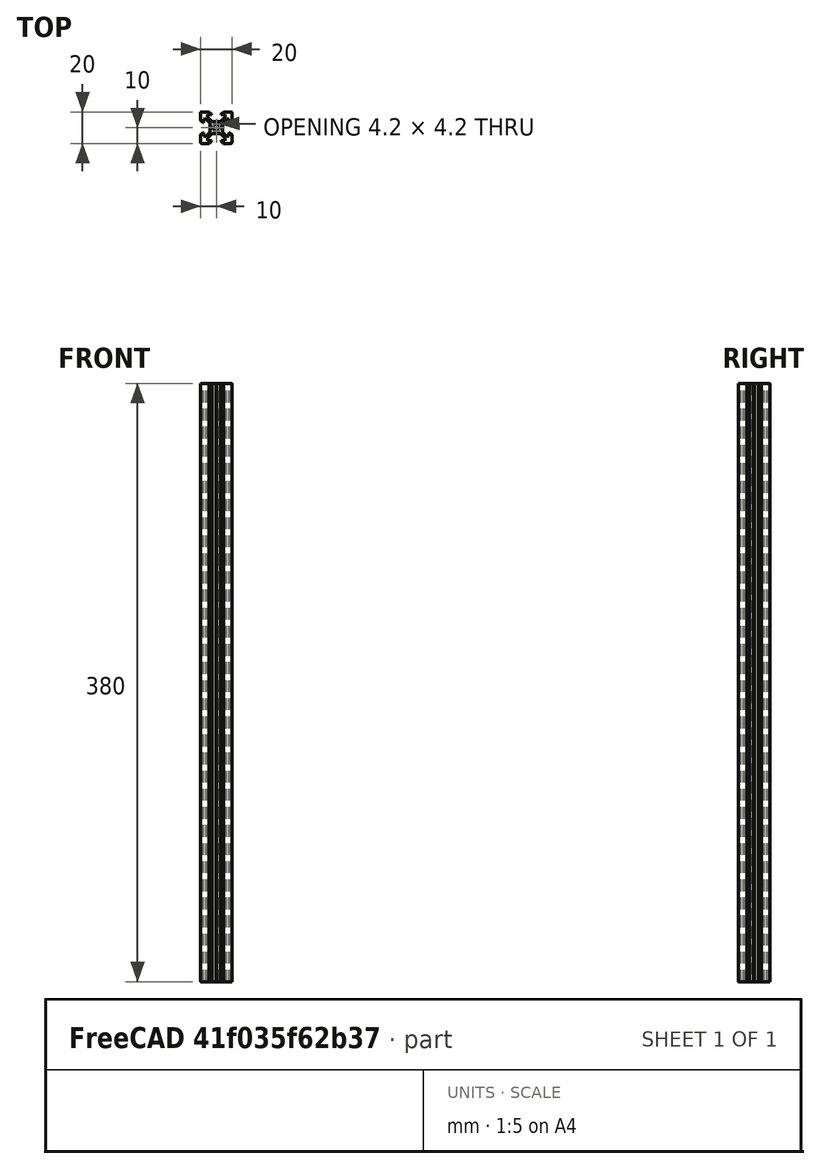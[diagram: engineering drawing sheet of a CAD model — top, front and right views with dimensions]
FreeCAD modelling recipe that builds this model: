
FCSTD DOCUMENT  (FreeCAD 0.19R23578 (Git))
Label: x_axis_rail
License: All rights reserved
LicenseURL: http://en.wikipedia.org/wiki/All_rights_reserved
objects: PartDesign::CoordinateSystem×3, Sketcher::SketchObject×1, PartDesign::Pad×1, PartDesign::Body×1, App::Part×1
note: 7 computed .brp shape members not serialized (recipe doc carries the construction recipe); baked Part::Feature solids carry a one-line shape summary decoded from their .brp

FEATURE [Sketcher::SketchObject] Sketch044
  Placement = pos=(0,0,0) rot=(0,1,0;3.14159rad)
  sketch-geometry (70):
    g0: LineSegment StartX=-3.69 StartY=1.29e-14 StartZ=0 EndX=-3.9 EndY=0.21 EndZ=0
    g1: LineSegment StartX=-3.69 StartY=1.29e-14 StartZ=0 EndX=-3.9 EndY=-0.21 EndZ=0
    g2: LineSegment StartX=-3.9 StartY=-0.21 StartZ=0 EndX=-3.9 EndY=-2.83934 EndZ=0
    g3: LineSegment StartX=-3.9 StartY=-2.83934 StartZ=0 EndX=-6.56066 EndY=-5.5 EndZ=0
    g4: LineSegment StartX=-6.56066 StartY=-5.5 StartZ=0 EndX=-8.2 EndY=-5.5 EndZ=0
    g5: LineSegment StartX=-8.2 StartY=-5.5 StartZ=0 EndX=-8.2 EndY=-3.125 EndZ=0
    g6: LineSegment StartX=-8.2 StartY=-3.125 StartZ=0 EndX=-8.545 EndY=-3.125 EndZ=0
    g7: LineSegment StartX=-8.545 StartY=-3.125 StartZ=0 EndX=-10 EndY=-4.58 EndZ=0
    g8: LineSegment StartX=-10 StartY=-4.58 StartZ=0 EndX=-10 EndY=-9.5 EndZ=0
    g9: ArcOfCircle CenterX=-9.5 CenterY=-9.5 CenterZ=0 NormalX=0 NormalY=0 NormalZ=1 AngleXU=-1e-16 Radius=0.5 StartAngle=3.14159 EndAngle=4.71239
    g10: LineSegment StartX=-9.5 StartY=-10 StartZ=0 EndX=-4.58 EndY=-10 EndZ=0
    g11: LineSegment StartX=-3.125 StartY=-8.545 StartZ=0 EndX=-4.58 EndY=-10 EndZ=0
    g12: LineSegment StartX=-3.125 StartY=-8.2 StartZ=0 EndX=-3.125 EndY=-8.545 EndZ=0
    g13: LineSegment StartX=-5.5 StartY=-8.2 StartZ=0 EndX=-3.125 EndY=-8.2 EndZ=0
    g14: LineSegment StartX=-5.5 StartY=-6.56066 StartZ=0 EndX=-5.5 EndY=-8.2 EndZ=0
    g15: LineSegment StartX=-2.83934 StartY=-3.9 StartZ=0 EndX=-5.5 EndY=-6.56066 EndZ=0
    g16: LineSegment StartX=-0.21 StartY=-3.9 StartZ=0 EndX=-2.83934 EndY=-3.9 EndZ=0
    g17: LineSegment StartX=-4e-16 StartY=-3.69 StartZ=0 EndX=-0.21 EndY=-3.9 EndZ=0
    g18: LineSegment StartX=-4e-16 StartY=-3.69 StartZ=0 EndX=0.21 EndY=-3.9 EndZ=0
    g19: LineSegment StartX=0.21 StartY=-3.9 StartZ=0 EndX=2.83934 EndY=-3.9 EndZ=0
    g20: LineSegment StartX=2.83934 StartY=-3.9 StartZ=0 EndX=5.5 EndY=-6.56066 EndZ=0
    g21: LineSegment StartX=5.5 StartY=-6.56066 StartZ=0 EndX=5.5 EndY=-8.2 EndZ=0
    g22: LineSegment StartX=5.5 StartY=-8.2 StartZ=0 EndX=3.125 EndY=-8.2 EndZ=0
    g23: LineSegment StartX=3.125 StartY=-8.2 StartZ=0 EndX=3.125 EndY=-8.545 EndZ=0
    g24: LineSegment StartX=3.125 StartY=-8.545 StartZ=0 EndX=4.58 EndY=-10 EndZ=0
    g25: LineSegment StartX=4.58 StartY=-10 StartZ=0 EndX=9.5 EndY=-10 EndZ=0
    g26: ArcOfCircle CenterX=9.5 CenterY=-9.5 CenterZ=0 NormalX=0 NormalY=0 NormalZ=1 AngleXU=-1e-16 Radius=0.5 StartAngle=4.71239 EndAngle=6.28319
    g27: LineSegment StartX=10 StartY=-4.58 StartZ=0 EndX=10 EndY=-9.5 EndZ=0
    g28: LineSegment StartX=8.545 StartY=-3.125 StartZ=0 EndX=10 EndY=-4.58 EndZ=0
    g29: LineSegment StartX=8.2 StartY=-3.125 StartZ=0 EndX=8.545 EndY=-3.125 EndZ=0
    g30: LineSegment StartX=8.2 StartY=-5.5 StartZ=0 EndX=8.2 EndY=-3.125 EndZ=0
    g31: LineSegment StartX=6.56066 StartY=-5.5 StartZ=0 EndX=8.2 EndY=-5.5 EndZ=0
    g32: LineSegment StartX=3.9 StartY=-2.83934 StartZ=0 EndX=6.56066 EndY=-5.5 EndZ=0
    g33: LineSegment StartX=3.9 StartY=-0.21 StartZ=0 EndX=3.9 EndY=-2.83934 EndZ=0
    g34: LineSegment StartX=3.69 StartY=1.18e-14 StartZ=0 EndX=3.9 EndY=-0.21 EndZ=0
    g35: LineSegment StartX=3.69 StartY=1.18e-14 StartZ=0 EndX=3.9 EndY=0.21 EndZ=0
    g36: LineSegment StartX=3.9 StartY=0.21 StartZ=0 EndX=3.9 EndY=2.83934 EndZ=0
    g37: LineSegment StartX=3.9 StartY=2.83934 StartZ=0 EndX=6.56066 EndY=5.5 EndZ=0
    g38: LineSegment StartX=6.56066 StartY=5.5 StartZ=0 EndX=8.2 EndY=5.5 EndZ=0
    g39: LineSegment StartX=8.2 StartY=5.5 StartZ=0 EndX=8.2 EndY=3.125 EndZ=0
    g40: LineSegment StartX=8.2 StartY=3.125 StartZ=0 EndX=8.545 EndY=3.125 EndZ=0
    g41: LineSegment StartX=8.545 StartY=3.125 StartZ=0 EndX=10 EndY=4.58 EndZ=0
    g42: LineSegment StartX=10 StartY=9.5 StartZ=0 EndX=10 EndY=4.58 EndZ=0
    g43: ArcOfCircle CenterX=9.5 CenterY=9.5 CenterZ=0 NormalX=0 NormalY=0 NormalZ=1 AngleXU=-1e-16 Radius=0.5 StartAngle=0 EndAngle=1.5708
    g44: LineSegment StartX=4.58 StartY=10 StartZ=0 EndX=9.5 EndY=10 EndZ=0
    g45: LineSegment StartX=3.125 StartY=8.545 StartZ=0 EndX=4.58 EndY=10 EndZ=0
    g46: LineSegment StartX=3.125 StartY=8.2 StartZ=0 EndX=3.125 EndY=8.545 EndZ=0
    g47: LineSegment StartX=5.5 StartY=8.2 StartZ=0 EndX=3.125 EndY=8.2 EndZ=0
    g48: LineSegment StartX=5.5 StartY=6.56066 StartZ=0 EndX=5.5 EndY=8.2 EndZ=0
    g49: LineSegment StartX=2.83934 StartY=3.9 StartZ=0 EndX=5.5 EndY=6.56066 EndZ=0
    g50: LineSegment StartX=0.21 StartY=3.9 StartZ=0 EndX=2.83934 EndY=3.9 EndZ=0
    g51: LineSegment StartX=-2.51e-14 StartY=3.69 StartZ=0 EndX=0.21 EndY=3.9 EndZ=0
    g52: LineSegment StartX=-2.51e-14 StartY=3.69 StartZ=0 EndX=-0.21 EndY=3.9 EndZ=0
    g53: LineSegment StartX=-0.21 StartY=3.9 StartZ=0 EndX=-2.83934 EndY=3.9 EndZ=0
    g54: LineSegment StartX=-2.83934 StartY=3.9 StartZ=0 EndX=-5.5 EndY=6.56066 EndZ=0
    g55: LineSegment StartX=-5.5 StartY=6.56066 StartZ=0 EndX=-5.5 EndY=8.2 EndZ=0
    g56: LineSegment StartX=-5.5 StartY=8.2 StartZ=0 EndX=-3.125 EndY=8.2 EndZ=0
    g57: LineSegment StartX=-3.125 StartY=8.2 StartZ=0 EndX=-3.125 EndY=8.545 EndZ=0
    g58: LineSegment StartX=-3.125 StartY=8.545 StartZ=0 EndX=-4.58 EndY=10 EndZ=0
    g59: LineSegment StartX=-9.5 StartY=10 StartZ=0 EndX=-4.58 EndY=10 EndZ=0
    g60: ArcOfCircle CenterX=-9.5 CenterY=9.5 CenterZ=0 NormalX=0 NormalY=0 NormalZ=1 AngleXU=-1e-16 Radius=0.5 StartAngle=1.5708 EndAngle=3.14159
    g61: LineSegment StartX=-10 StartY=9.5 StartZ=0 EndX=-10 EndY=4.58 EndZ=0
    g62: LineSegment StartX=-8.545 StartY=3.125 StartZ=0 EndX=-10 EndY=4.58 EndZ=0
    g63: LineSegment StartX=-8.2 StartY=3.125 StartZ=0 EndX=-8.545 EndY=3.125 EndZ=0
    g64: LineSegment StartX=-8.2 StartY=5.5 StartZ=0 EndX=-8.2 EndY=3.125 EndZ=0
    g65: LineSegment StartX=-6.56066 StartY=5.5 StartZ=0 EndX=-8.2 EndY=5.5 EndZ=0
    g66: LineSegment StartX=-3.9 StartY=2.83934 StartZ=0 EndX=-6.56066 EndY=5.5 EndZ=0
    g67: LineSegment StartX=-3.9 StartY=0.21 StartZ=0 EndX=-3.9 EndY=2.83934 EndZ=0
    g68: ArcOfCircle CenterX=0 CenterY=0 CenterZ=0 NormalX=0 NormalY=0 NormalZ=1 AngleXU=-1e-16 Radius=2.1 StartAngle=3.14159 EndAngle=6.28319
    g69: ArcOfCircle CenterX=0 CenterY=0 CenterZ=0 NormalX=0 NormalY=0 NormalZ=1 AngleXU=-1e-16 Radius=2.1 StartAngle=0 EndAngle=3.14159
  constraints (149):
    c: Coincident(g0,g1)
    c: Coincident(g1,g2)
    c: Coincident(g2,g3)
    c: Coincident(g3,g4)
    c: Coincident(g4,g5)
    c: Coincident(g5,g6)
    c: Coincident(g6,g7)
    c: Coincident(g7,g8)
    c: Coincident(g8,g9)
    c: Coincident(g9,g10)
    c: Coincident(g10,g11)
    c: Coincident(g11,g12)
    c: Vertical(g12)
    c: Coincident(g12,g13)
    c: Horizontal(g13)
    c: Coincident(g13,g14)
    c: Vertical(g14)
    c: Coincident(g14,g15)
    c: Coincident(g15,g16)
    c: Coincident(g16,g17)
    c: Coincident(g17,g18)
    c: Coincident(g18,g19)
    c: Horizontal(g19)
    c: Coincident(g19,g20)
    c: Coincident(g20,g21)
    c: Vertical(g21)
    c: Coincident(g21,g22)
    c: Horizontal(g22)
    c: Coincident(g22,g23)
    c: Vertical(g23)
    c: Coincident(g23,g24)
    c: Coincident(g24,g25)
    c: Coincident(g25,g26)
    c: Coincident(g26,g27)
    c: Coincident(g27,g28)
    c: Coincident(g28,g29)
    c: Coincident(g29,g30)
    c: Coincident(g30,g31)
    c: Coincident(g31,g32)
    c: Coincident(g32,g33)
    c: Coincident(g33,g34)
    c: Coincident(g34,g35)
    c: Coincident(g35,g36)
    c: Coincident(g36,g37)
    c: Coincident(g37,g38)
    c: Coincident(g38,g39)
    c: Coincident(g39,g40)
    c: Coincident(g40,g41)
    c: Coincident(g41,g42)
    c: Coincident(g42,g43)
    c: Coincident(g43,g44)
    c: Horizontal(g44)
    c: Coincident(g44,g45)
    c: Coincident(g45,g46)
    c: Coincident(g46,g47)
    c: Coincident(g47,g48)
    c: Coincident(g48,g49)
    c: Coincident(g49,g50)
    c: Coincident(g50,g51)
    c: Coincident(g51,g52)
    c: Coincident(g52,g53)
    c: Coincident(g53,g54)
    c: Coincident(g54,g55)
    c: Coincident(g55,g56)
    c: Coincident(g56,g57)
    c: Coincident(g57,g58)
    c: Coincident(g58,g59)
    c: Horizontal(g59)
    c: Coincident(g59,g60)
    c: Coincident(g60,g61)
    c: Coincident(g61,g62)
    c: Coincident(g62,g63)
    c: Coincident(g63,g64)
    c: Coincident(g64,g65)
    c: Coincident(g65,g66)
    c: Coincident(g66,g67)
    c: Coincident(g67,g0)
    c: Coincident(g68,g69)
    c: Coincident(g69,g68)
    c: Block(g30)
    c: Block(g29)
    c: Block(g28)
    c: Block(g27)
    c: Block(g31)
    c: Block(g32)
    c: Block(g33)
    c: Block(g34)
    c: Block(g35)
    c: Block(g36)
    c: Block(g69)
    c: Block(g68)
    c: Block(g37)
    c: Block(g38)
    c: Block(g39)
    c: Block(g40)
    c: Block(g41)
    c: Block(g42)
    c: Block(g43)
    c: Block(g44)
    c: Block(g45)
    c: Block(g46)
    c: Block(g47)
    c: Block(g48)
    c: Block(g49)
    c: Block(g50)
    c: Block(g53)
    c: Block(g52)
    c: Block(g51)
    c: Block(g54)
    c: Block(g55)
    c: Block(g56)
    c: Block(g57)
    c: Block(g58)
    c: Block(g59)
    c: Block(g60)
    c: Block(g61)
    c: Block(g62)
    c: Block(g63)
    c: Block(g64)
    c: Block(g65)
    c: Block(g66)
    c: Block(g67)
    c: Block(g0)
    c: Block(g1)
    c: Block(g2)
    c: Block(g3)
    c: Block(g4)
    c: Block(g5)
    c: Block(g6)
    c: Block(g7)
    c: Block(g8)
    c: Block(g9)
    c: Block(g10)
    c: Block(g11)
    c: Block(g12)
    c: Block(g13)
    c: Block(g14)
    c: Block(g15)
    c: Block(g16)
    c: Block(g17)
    c: Block(g18)
    c: Block(g19)
    c: Block(g20)
    c: Block(g21)
    c: Block(g22)
    c: Block(g23)
    c: Block(g24)
    c: Block(g25)
    c: Block(g26)
FEATURE [PartDesign::Pad] Pad018
  AllowMultiFace = false
  Direction = (1,1,1)
  Length = 380
  Length2 = 100
  Placement = pos=(0,0,0) rot=(0,1,0;3.14159rad)
  Profile = -> Sketch044
  Reversed = true
  Type = 0
FEATURE [PartDesign::Body] Body017  label="Body"
  Group = -> [Sketch044,Pad018]
  Origin = -> Origin047
  Tip = -> Pad018
FEATURE [PartDesign::CoordinateSystem] LCS_1
  AttacherType = Attacher::AttachEngine3D
  MapMode = 45
  Placement = pos=(1e-16,-1e-16,380) rot=(0,0,1;0rad)
  Support = -> [Pad018]
FEATURE [PartDesign::CoordinateSystem] LCS_2
  AttacherType = Attacher::AttachEngine3D
  MapMode = 45
  Placement = pos=(-10,-3.9e-14,0) rot=(0,0.707107,0.707107;3.14159rad)
  Support = -> [Pad018]
FEATURE [PartDesign::CoordinateSystem] LCS_3
  AttacherType = Attacher::AttachEngine3D
  MapMode = 45
  Placement = pos=(1e-16,-1e-16,190) rot=(0,0,1;0rad)
  Support = -> [Pad018]
FEATURE [App::Part] Part028  label="2020_vslot_rail"
  Group = -> [Body017,LCS_1,LCS_2,LCS_3]
  Origin = -> Origin042
